# Revit family: NXRO
name_source: partatom
category: Communication Devices
units: mm (PartAtom-declared; Revit-internal decimal feet)

## family parameters
Cut with Voids When Loaded = No
Host = Face
Maintain Annotation Orientation = No
OmniClass Number = 23.85.80.11.27
OmniClass Title = Lighting Controls
Part Type = Normal
Room Calculation Point = No
Round Connector Dimension = Use Diameter
Shared = Yes

## types (1)
- NXRO
    Apparent Load = 0 VA
    Assembly Code = D5090
    Black Material = Paint - Black Matte Textured
    Default Elevation = 48 "
    Description = The NX Occupancy Output Interface provides a means to
communicate the occupancy state of an NX distributed control
zone to HVAC or other systems using simple contact closure. The
NXRO connects to the SmartPORT™ and provides the aggregate
occupancy state of the zone as reported by one or more
occupancy sensors.
    Features = • Mounts to standard 4 11/16" junction box, Raco #257 or similar
• Removable terminal bloc for input connection
• Connects to and is powered by NX SmartPORT
• Supports multiple occupancy sensors in the zone
• Low voltage Form C output relay supports NC and NO operation
• Low voltage device: 24 VDC
    Green Element = Plastic -  Green
    Manufacturer = NX Lighting Controls
    Model = NXRO
    Steel = Metal-Galvanized_Steel
    Type Comments = NX Occupancy Output Interface
    URL = https://www.currentlighting.com
    Voltage = 24 V
    Warranty = 5-Years Warranty
    White Element = Glass, White, High Luminance

## geometry (parser evidence)
native form markers: Sweep x3
no freeform markers — native parametric forms only
